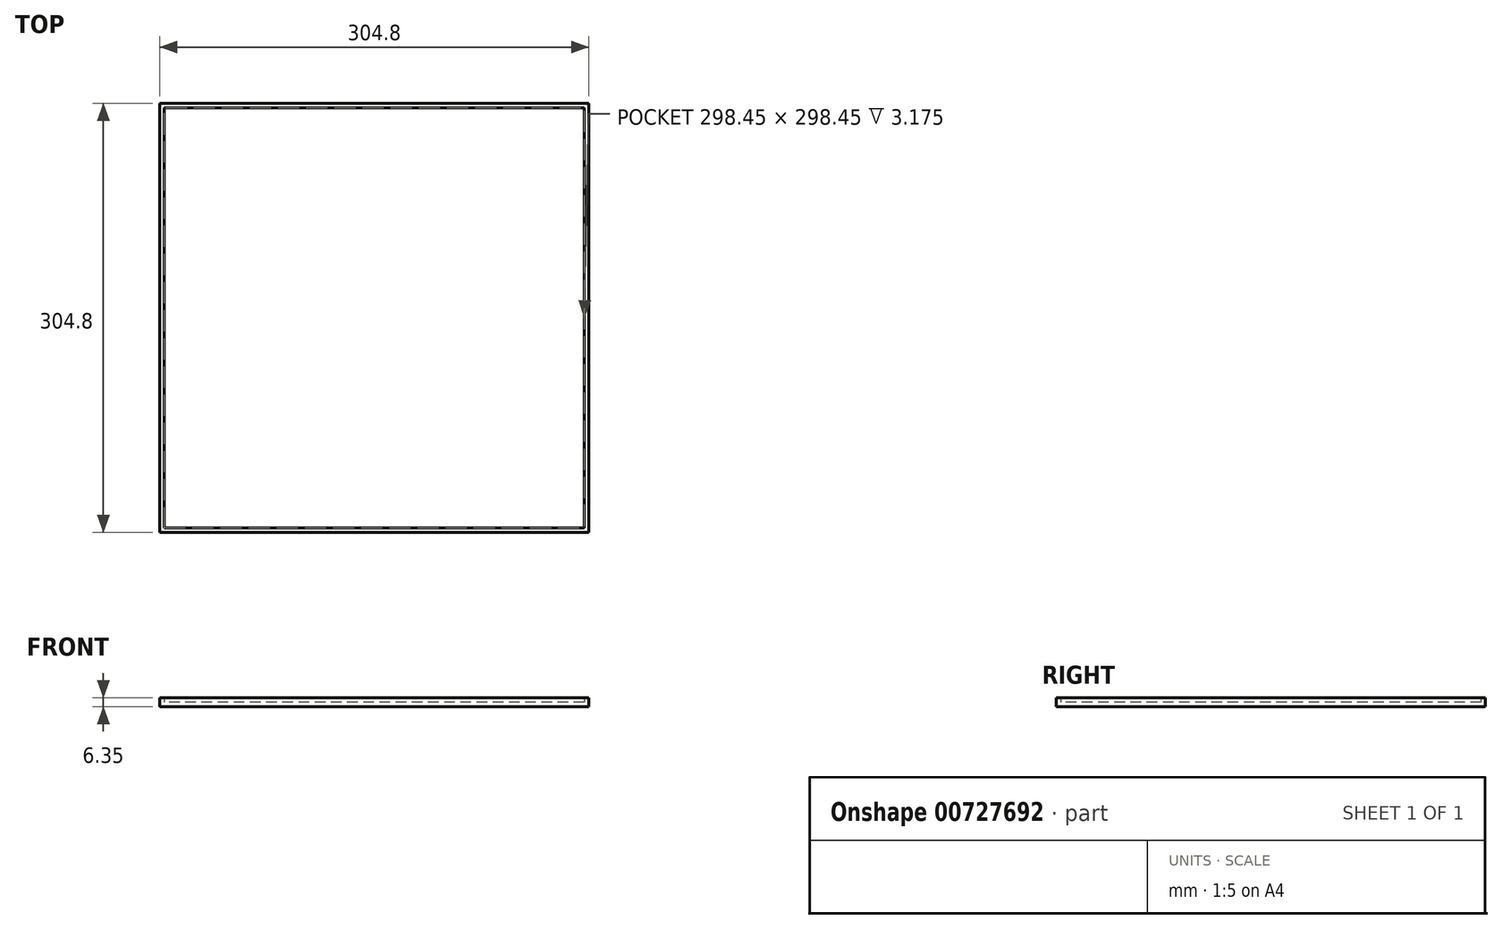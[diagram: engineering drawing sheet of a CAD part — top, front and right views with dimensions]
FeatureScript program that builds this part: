
annotation { "Feature Type Name" : "Feature", "Feature Type Description" : "" }
export const myFeature = defineFeature(function(context is Context, id is Id, definition is map)
    precondition{}
    {
        {
            var Q0;
            Q0=qCreatedBy(makeId("Top.planeOp"),FACE);
            var sketch = newSketch(context, id + "F0", { "sketchPlane" : qUnion([Q0])});
            skLineSegment(sketch, "E0.bottom", {"start": v(152.4, 152.4) * mm, "end": v(-152.4, 152.4) * mm});
            skLineSegment(sketch, "E0.top", {"start": v(152.4, -152.4) * mm, "end": v(-152.4, -152.4) * mm});
            skLineSegment(sketch, "E0.left", {"start": v(152.4, 152.4) * mm, "end": v(152.4, -152.4) * mm});
            skLineSegment(sketch, "E0.right", {"start": v(-152.4, 152.4) * mm, "end": v(-152.4, -152.4) * mm});
            skPoint(sketch, "E0.middle", {"position": v(0, 0) * mm});
            skSolve(sketch);
        }
        {
            var Q0;
            Q0 = qSketchRegion(id + "F0", true);
            extrude(context, id + "F1", {"entities" : qUnion([Q0]), "depth" : 3.17 * mm, "offsetDistance" : 25.4 * mm});
        }
        {
            var Q0;
            Q0=makeQuery(id+"F1.opExtrude","CAP_FACE",FACE,{"disambiguationData":[OSD([sQuery(id+"F0.wireOp",EDGE,"E0.bottom"),sQuery(id+"F0.wireOp",EDGE,"E0.top"),sQuery(id+"F0.wireOp",EDGE,"E0.left"),sQuery(id+"F0.wireOp",EDGE,"E0.right")])],"isStart":false});
            var sketch = newSketch(context, id + "F2", { "sketchPlane" : qUnion([Q0])});
            skLineSegment(sketch, "E1.0", {"start": v(152.4, 152.4) * mm, "end": v(-152.4, 152.4) * mm});
            skLineSegment(sketch, "E1.1", {"start": v(-152.4, 152.4) * mm, "end": v(-152.4, -152.4) * mm});
            skLineSegment(sketch, "E1.2", {"start": v(152.4, -152.4) * mm, "end": v(-152.4, -152.4) * mm});
            skLineSegment(sketch, "E1.3", {"start": v(152.4, 152.4) * mm, "end": v(152.4, -152.4) * mm});
            skLineSegment(sketch, "E2.0", {"start": v(149.22, 149.22) * mm, "end": v(-149.22, 149.22) * mm});
            skLineSegment(sketch, "E2.1", {"start": v(149.22, 149.22) * mm, "end": v(149.22, -149.22) * mm});
            skLineSegment(sketch, "E2.2", {"start": v(149.22, -149.22) * mm, "end": v(-149.22, -149.22) * mm});
            skLineSegment(sketch, "E2.3", {"start": v(-149.22, 149.22) * mm, "end": v(-149.22, -149.22) * mm});
            skSolve(sketch);
        }
        {
            var Q0;
            Q0 = qSketchRegion(id + "F2", true);
            extrude(context, id + "F3", {"entities" : qUnion([Q0]), "operationType" : NewBodyOperationType.ADD, "depth" : 3.17 * mm, "offsetDistance" : 25.4 * mm});
        }
    });
